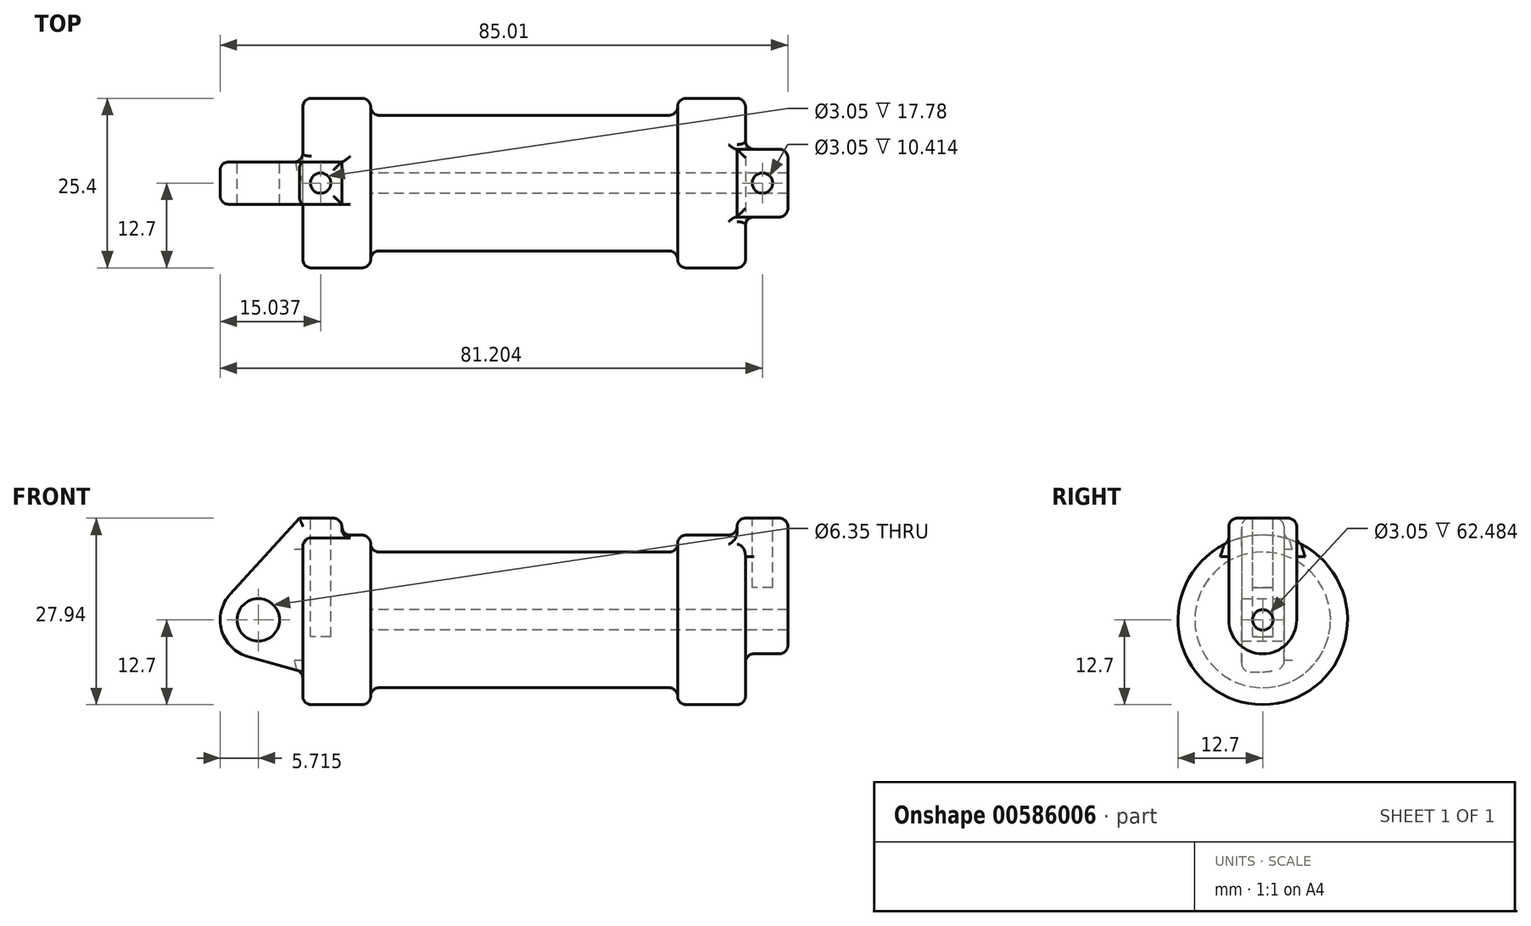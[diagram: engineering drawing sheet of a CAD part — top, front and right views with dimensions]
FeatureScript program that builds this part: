
annotation { "Feature Type Name" : "Feature", "Feature Type Description" : "" }
export const myFeature = defineFeature(function(context is Context, id is Id, definition is map)
    precondition{}
    {
        {
            var Q0;
            Q0=qCreatedBy(makeId("Front.planeOp"),FACE);
            var sketch = newSketch(context, id + "F0", { "sketchPlane" : qUnion([Q0])});
            skLineSegment(sketch, "E0", {"start": v(0, 0) * mm, "end": v(0, 12.7) * mm});
            skLineSegment(sketch, "E1", {"start": v(0, 12.7) * mm, "end": v(10.16, 12.7) * mm});
            skLineSegment(sketch, "E2", {"start": v(10.16, 12.7) * mm, "end": v(10.16, 10.16) * mm});
            skLineSegment(sketch, "E3", {"start": v(10.16, 10.16) * mm, "end": v(56.13, 10.16) * mm});
            skLineSegment(sketch, "E4", {"start": v(56.13, 10.16) * mm, "end": v(56.13, 12.7) * mm});
            skLineSegment(sketch, "E5", {"start": v(56.13, 12.7) * mm, "end": v(66.3, 12.7) * mm});
            skLineSegment(sketch, "E6", {"start": v(66.3, 12.7) * mm, "end": v(66.3, 0) * mm});
            skLineSegment(sketch, "E7", {"start": v(66.3, 0) * mm, "end": v(0, 0) * mm});
            skLineSegment(sketch, "E8", {"start": v(5.84, 15.24) * mm, "end": v(-0.5, 15.24) * mm});
            skLineSegment(sketch, "E9", {"start": v(-0.5, 15.24) * mm, "end": v(-10.88, 3.85) * mm});
            skLineSegment(sketch, "E10", {"start": v(0, 0) * mm, "end": v(-6.65, 0) * mm});
            skCircle(sketch, "E11", {"center": v(-6.65, 0) * mm, "radius": 5.72 * mm});
            skCircle(sketch, "E12", {"center": v(-6.65, 0) * mm, "radius": 3.18 * mm});
            skLineSegment(sketch, "E13", {"start": v(5.84, 15.24) * mm, "end": v(5.84, -9.4) * mm});
            skLineSegment(sketch, "E14", {"start": v(5.84, -9.4) * mm, "end": v(-8.18, -5.5) * mm});
            skSolve(sketch);
        }
        {
            var Q0;
            {var subQ0=sQuery(id+"F0.wireOp",EDGE,"E2");Q0=makeQuery(id+"F0.imprint","IMPRINT",FACE,{"disambiguationData":[TD([[makeQuery(id+"F0.imprint","IMPRINT",EDGE,{"derivedFrom":subQ0}),-1.0]])]});}
            var Q1;
            {var subQ0=sQuery(id+"F0.wireOp",EDGE,"E0");Q1=makeQuery(id+"F0.imprint","IMPRINT",FACE,{"disambiguationData":[TD([[makeQuery(id+"F0.imprint","IMPRINT",EDGE,{"derivedFrom":subQ0}),-1.0]])]});}
            var Q2;
            Q2=sQuery(id+"F0.wireOp",EDGE,"E7");
            revolve(context, id + "F1", {"entities" : qUnion([Q0, Q1]), "axis" : qUnion([Q2]), "revolveType" : RevolveType.FULL});
        }
        {
            var Q0;
            {var subQ1=sQuery(id+"F0.wireOp",EDGE,"E0");Q0=makeQuery(id+"F0.imprint","IMPRINT",FACE,{"disambiguationData":[TD([[makeQuery(id+"F0.imprint","IMPRINT",EDGE,{"derivedFrom":subQ1}),1.0]])]});}
            var Q1;
            {var subQ5=sQuery(id+"F0.wireOp",EDGE,"E12");Q1=makeQuery(id+"F0.imprint","IMPRINT",FACE,{"disambiguationData":[TD([[makeQuery(id+"F0.imprint","IMPRINT",EDGE,{"derivedFrom":subQ5}),-1.0]])]});}
            var Q2;
            {var subQ0=sQuery(id+"F0.wireOp",EDGE,"E14");Q2=makeQuery(id+"F0.imprint","IMPRINT",FACE,{"disambiguationData":[TD([[makeQuery(id+"F0.imprint","IMPRINT",EDGE,{"derivedFrom":subQ0}),-1.0]])]});}
            var Q3;
            {var subQ0=sQuery(id+"F0.wireOp",EDGE,"E0");Q3=makeQuery(id+"F0.imprint","IMPRINT",FACE,{"disambiguationData":[TD([[makeQuery(id+"F0.imprint","IMPRINT",EDGE,{"derivedFrom":subQ0}),-1.0]])]});}
            extrude(context, id + "F2", {"entities" : qUnion([Q0, Q1, Q2, Q3]), "operationType" : NewBodyOperationType.ADD, "endBound" : BoundingType.SYMMETRIC, "depth" : 6.35 * mm, "offsetDistance" : 25.4 * mm});
        }
        {
            var Q0;
            Q0=makeQuery(id+"F1.opRevolve","SWEPT_FACE",FACE,{"disambiguationData":[OSD([sQuery(id+"F0.wireOp",EDGE,"E6")])]});
            var sketch = newSketch(context, id + "F3", { "sketchPlane" : qUnion([Q0])});
            skCircle(sketch, "E15", {"center": v(0, 0) * mm, "radius": 1.52 * mm});
            skCircle(sketch, "E16", {"center": v(0, 0) * mm, "radius": 5.08 * mm});
            skLineSegment(sketch, "E17", {"start": v(-5.08, 0) * mm, "end": v(-5.08, 15.24) * mm});
            skLineSegment(sketch, "E18", {"start": v(-5.08, 15.24) * mm, "end": v(5.08, 15.24) * mm});
            skLineSegment(sketch, "E19", {"start": v(5.08, 15.24) * mm, "end": v(5.08, 0) * mm});
            skSolve(sketch);
        }
        {
            var Q0;
            {var subQ0=sQuery(id+"F3.wireOp",EDGE,"E18");Q0=makeQuery(id+"F3.imprint","IMPRINT",FACE,{"disambiguationData":[TD([[makeQuery(id+"F3.imprint","IMPRINT",EDGE,{"derivedFrom":subQ0}),-1.0]])]});}
            var Q1;
            {var subQ0=sQuery(id+"F3.wireOp",EDGE,"E17");var subQ1=sQuery(id+"F3.wireOp",EDGE,"E16");var subQ2=makeQuery(id+"F3.imprint","INTERSECT",VERTEX,{"derivedFrom":[subQ1,subQ0]});Q1=makeQuery(id+"F3.imprint","IMPRINT",FACE,{"disambiguationData":[TD([[makeQuery(id+"F3.imprint","IMPRINT",EDGE,{"disambiguationData":[TD([[subQ2,1.0]])],"derivedFrom":subQ1}),-1.0]])]});}
            var Q2;
            Q2=makeQuery(id+"F3.imprint","IMPRINT",FACE,{"disambiguationData":[TD([[makeQuery(id+"F3.imprint","IMPRINT",EDGE,{"derivedFrom":sQuery(id+"F3.wireOp",EDGE,"E15")}),-1.0]])]});
            extrude(context, id + "F4", {"entities" : qUnion([Q0, Q1, Q2]), "operationType" : NewBodyOperationType.ADD, "depth" : 6.35 * mm, "offsetDistance" : 25.4 * mm});
        }
        {
            var Q0;
            Q0 = qSketchRegion(id + "F3", true);
            extrude(context, id + "F5", {"entities" : qUnion([Q0]), "operationType" : NewBodyOperationType.ADD, "oppositeDirection" : true, "depth" : 1.27 * mm, "offsetDistance" : 25.4 * mm});
        }
        {
            var Q0;
            Q0=makeQuery(id+"F4.boolean.opBoolean","SPLIT",FACE,{"disambiguationData":[TD([makeQuery(id+"F4.opExtrude","SWEPT_FACE",FACE,{"disambiguationData":[OSD([sQuery(id+"F3.wireOp",EDGE,"E15")])]})])],"derivedFrom":makeQuery(id+"F1.opRevolve","SWEPT_FACE",FACE,{"disambiguationData":[OSD([sQuery(id+"F0.wireOp",EDGE,"E6")])]})});
            var Q1;
            Q1=makeQuery(id+"F1.opRevolve","SWEPT_FACE",FACE,{"disambiguationData":[OSD([sQuery(id+"F0.wireOp",EDGE,"E2")])]});
            extrude(context, id + "F6", {"entities" : qUnion([Q0]), "operationType" : NewBodyOperationType.REMOVE, "endBound" : BoundingType.UP_TO_SURFACE, "oppositeDirection" : true, "depth" : 25.4 * mm, "endBoundEntityFace" : qUnion([Q1]), "offsetDistance" : 25.4 * mm});
        }
        {
            var Q0;
            Q0=makeQuery(id+"F2.opExtrude","SWEPT_FACE",FACE,{"disambiguationData":[OSD([sQuery(id+"F0.wireOp",EDGE,"E8")])]});
            var sketch = newSketch(context, id + "F7", { "sketchPlane" : qUnion([Q0])});
            skCircle(sketch, "E20", {"center": v(2.67, 0) * mm, "radius": 1.52 * mm});
            skPoint(sketch, "E20.centerSnap0", {"position": v(2.67, 3.18) * mm});
            skPoint(sketch, "E20.centerSnap1", {"position": v(5.84, 0) * mm});
            skSolve(sketch);
        }
        {
            var Q0;
            Q0=makeQuery(id+"F7.imprint","IMPRINT",FACE,{"disambiguationData":[TD([[makeQuery(id+"F7.imprint","IMPRINT",EDGE,{"derivedFrom":sQuery(id+"F7.wireOp",EDGE,"E20")}),1.0]])]});
            extrude(context, id + "F8", {"entities" : qUnion([Q0]), "operationType" : NewBodyOperationType.REMOVE, "oppositeDirection" : true, "depth" : 17.78 * mm, "offsetDistance" : 25.4 * mm});
        }
        {
            var Q0;
            {var subQ0=sQuery(id+"F3.wireOp",EDGE,"E18");Q0=makeQuery(id+"F5.boolean.opBoolean","MERGE",FACE,{"derivedFrom":[makeQuery(id+"F4.opExtrude","SWEPT_FACE",FACE,{"disambiguationData":[OSD([subQ0])]}),makeQuery(id+"F5.opExtrude","SWEPT_FACE",FACE,{"disambiguationData":[OSD([subQ0])]})]});}
            var sketch = newSketch(context, id + "F9", { "sketchPlane" : qUnion([Q0])});
            skCircle(sketch, "E21", {"center": v(68.83, 0) * mm, "radius": 1.52 * mm});
            skPoint(sketch, "E21.centerSnap0", {"position": v(72.64, 0) * mm});
            skPoint(sketch, "E21.centerSnap1", {"position": v(68.83, 5.08) * mm});
            skSolve(sketch);
        }
        {
            var Q0;
            Q0=makeQuery(id+"F9.imprint","IMPRINT",FACE,{"disambiguationData":[TD([[makeQuery(id+"F9.imprint","IMPRINT",EDGE,{"derivedFrom":sQuery(id+"F9.wireOp",EDGE,"E21")}),1.0]])]});
            extrude(context, id + "F10", {"entities" : qUnion([Q0]), "operationType" : NewBodyOperationType.REMOVE, "oppositeDirection" : true, "depth" : 10.4 * mm, "offsetDistance" : 25.4 * mm});
        }
        {
            var Q0;
            {var subQ0=sQuery(id+"F0.wireOp",EDGE,"E5");var subQ1=sQuery(id+"F0.wireOp",EDGE,"E6");Q0=makeQuery(id+"F4.boolean.opBoolean","SPLIT",EDGE,{"disambiguationData":[topologyDisambiguationEdgeConnected([makeQuery(id+"F1.opRevolve","SWEPT_FACE",FACE,{"disambiguationData":[OSD([subQ1])]})])],"derivedFrom":makeQuery(id+"F1.opRevolve","SWEPT_EDGE",EDGE,{"disambiguationData":[OSD([subQ0,subQ1])]})});}
            var Q1;
            Q1=makeQuery(id+"F1.opRevolve","SWEPT_EDGE",EDGE,{"disambiguationData":[OSD([sQuery(id+"F0.wireOp",EDGE,"E4"),sQuery(id+"F0.wireOp",EDGE,"E5")])]});
            var Q2;
            Q2=makeQuery(id+"F1.opRevolve","SWEPT_EDGE",EDGE,{"disambiguationData":[OSD([sQuery(id+"F0.wireOp",EDGE,"E1"),sQuery(id+"F0.wireOp",EDGE,"E2")])]});
            var Q3;
            Q3=makeQuery(id+"F1.opRevolve","SWEPT_EDGE",EDGE,{"disambiguationData":[OSD([sQuery(id+"F0.wireOp",EDGE,"E0"),sQuery(id+"F0.wireOp",EDGE,"E1")])]});
            var Q4;
            Q4=makeQuery(id+"F1.opRevolve","SWEPT_EDGE",EDGE,{"disambiguationData":[OSD([sQuery(id+"F0.wireOp",EDGE,"E2"),sQuery(id+"F0.wireOp",EDGE,"E3")])]});
            var Q5;
            Q5=makeQuery(id+"F1.opRevolve","SWEPT_EDGE",EDGE,{"disambiguationData":[OSD([sQuery(id+"F0.wireOp",EDGE,"E3"),sQuery(id+"F0.wireOp",EDGE,"E4")])]});
            fillet(context, id + "F11", {"entities" : qUnion([Q0, Q1, Q2, Q3, Q4, Q5]), "radius" : 1.27 * mm, "tangentPropagation" : true, "allowEdgeOverflow" : false});
        }
        {
            var Q0;
            Q0=makeQuery(id+"F4.opExtrude","CAP_EDGE",EDGE,{"disambiguationData":[OSD([sQuery(id+"F3.wireOp",EDGE,"E18")])],"isStart":false});
            var Q1;
            {var subQ0=sQuery(id+"F3.wireOp",EDGE,"E18");var subQ1=sQuery(id+"F3.wireOp",EDGE,"E17");Q1=makeQuery(id+"F5.boolean.opBoolean","MERGE",EDGE,{"derivedFrom":[makeQuery(id+"F4.opExtrude","SWEPT_EDGE",EDGE,{"disambiguationData":[OSD([subQ1,subQ0])]}),makeQuery(id+"F5.opExtrude","SWEPT_EDGE",EDGE,{"disambiguationData":[OSD([subQ1,subQ0])]})]});}
            var Q2;
            Q2=makeQuery(id+"F4.opExtrude","CAP_EDGE",EDGE,{"disambiguationData":[OSD([sQuery(id+"F3.wireOp",EDGE,"E17")])],"isStart":false});
            var Q3;
            Q3=makeQuery(id+"F4.opExtrude","CAP_EDGE",EDGE,{"disambiguationData":[OSD([sQuery(id+"F3.wireOp",EDGE,"E16")])],"isStart":false});
            var Q4;
            {var subQ0=sQuery(id+"F3.wireOp",EDGE,"E17");Q4=makeQuery(id+"F4.boolean.opBoolean","SPLIT",EDGE,{"disambiguationData":[topologyDisambiguationEdgeConnected([makeQuery(id+"F1.opRevolve","SWEPT_FACE",FACE,{"disambiguationData":[OSD([sQuery(id+"F0.wireOp",EDGE,"E6")])]})])],"derivedFrom":makeQuery(id+"F4.opExtrude","CAP_EDGE",EDGE,{"disambiguationData":[OSD([subQ0])],"isStart":true})});}
            var Q5;
            {var subQ0=sQuery(id+"F3.wireOp",EDGE,"E17");var subQ1=sQuery(id+"F0.wireOp",EDGE,"E5");var subQ2=sQuery(id+"F0.wireOp",EDGE,"E6");Q5=makeQuery(id+"F11.opFillet","BLEND_EDGE",EDGE,{"blendedFrom":[makeQuery(id+"F4.boolean.opBoolean","SPLIT",EDGE,{"disambiguationData":[topologyDisambiguationEdgeConnected([makeQuery(id+"F1.opRevolve","SWEPT_FACE",FACE,{"disambiguationData":[OSD([subQ2])]})])],"derivedFrom":makeQuery(id+"F1.opRevolve","SWEPT_EDGE",EDGE,{"disambiguationData":[OSD([subQ1,subQ2])]})}),makeQuery(id+"F5.boolean.opBoolean","MERGE",FACE,{"derivedFrom":[makeQuery(id+"F4.opExtrude","SWEPT_FACE",FACE,{"disambiguationData":[OSD([subQ0])]}),makeQuery(id+"F5.opExtrude","SWEPT_FACE",FACE,{"disambiguationData":[OSD([subQ0])]})]})],"blendedInto":[makeQuery(id+"F5.boolean.opBoolean","MERGE",FACE,{"derivedFrom":[makeQuery(id+"F4.opExtrude","SWEPT_FACE",FACE,{"disambiguationData":[OSD([subQ0])]}),makeQuery(id+"F5.opExtrude","SWEPT_FACE",FACE,{"disambiguationData":[OSD([subQ0])]})]})]});}
            var Q6;
            Q6=makeQuery(id+"F5.boolean.opBoolean","INTERSECT",EDGE,{"derivedFrom":[makeQuery(id+"F1.opRevolve","SWEPT_FACE",FACE,{"disambiguationData":[OSD([sQuery(id+"F0.wireOp",EDGE,"E5")])]}),makeQuery(id+"F5.opExtrude","CAP_FACE",FACE,{"disambiguationData":[OSD([sQuery(id+"F3.wireOp",EDGE,"E15"),sQuery(id+"F3.wireOp",EDGE,"E16"),sQuery(id+"F3.wireOp",EDGE,"E17"),sQuery(id+"F3.wireOp",EDGE,"E18"),sQuery(id+"F3.wireOp",EDGE,"E19")])],"isStart":false})]});
            var Q7;
            {var subQ0=sQuery(id+"F3.wireOp",EDGE,"E19");var subQ1=sQuery(id+"F3.wireOp",EDGE,"E18");Q7=makeQuery(id+"F5.boolean.opBoolean","MERGE",EDGE,{"derivedFrom":[makeQuery(id+"F4.opExtrude","SWEPT_EDGE",EDGE,{"disambiguationData":[OSD([subQ1,subQ0])]}),makeQuery(id+"F5.opExtrude","SWEPT_EDGE",EDGE,{"disambiguationData":[OSD([subQ1,subQ0])]})]});}
            var Q8;
            Q8=makeQuery(id+"F5.opExtrude","CAP_EDGE",EDGE,{"disambiguationData":[OSD([sQuery(id+"F3.wireOp",EDGE,"E18")])],"isStart":false});
            fillet(context, id + "F12", {"entities" : qUnion([Q0, Q1, Q2, Q3, Q4, Q5, Q6, Q7, Q8]), "radius" : 1.27 * mm, "tangentPropagation" : true, "allowEdgeOverflow" : false});
        }
        {
            var Q0;
            Q0=makeQuery(id+"F2.opExtrude","CAP_EDGE",EDGE,{"disambiguationData":[OSD([sQuery(id+"F0.wireOp",EDGE,"E9")])],"isStart":false});
            var Q1;
            Q1=makeQuery(id+"F2.opExtrude","CAP_EDGE",EDGE,{"disambiguationData":[OSD([sQuery(id+"F0.wireOp",EDGE,"E11")])],"isStart":false});
            var Q2;
            Q2=makeQuery(id+"F2.opExtrude","CAP_EDGE",EDGE,{"disambiguationData":[OSD([sQuery(id+"F0.wireOp",EDGE,"E8")])],"isStart":false});
            var Q3;
            Q3=makeQuery(id+"F2.opExtrude","SWEPT_EDGE",EDGE,{"disambiguationData":[OSD([sQuery(id+"F0.wireOp",EDGE,"E8"),sQuery(id+"F0.wireOp",EDGE,"E13")])]});
            var Q4;
            Q4=makeQuery(id+"F2.opExtrude","CAP_EDGE",EDGE,{"disambiguationData":[OSD([sQuery(id+"F0.wireOp",EDGE,"E8")])],"isStart":true});
            var Q5;
            Q5=makeQuery(id+"F2.opExtrude","CAP_EDGE",EDGE,{"disambiguationData":[OSD([sQuery(id+"F0.wireOp",EDGE,"E9")])],"isStart":true});
            var Q6;
            Q6=makeQuery(id+"F2.boolean.opBoolean","INTERSECT",EDGE,{"derivedFrom":[makeQuery(id+"F1.opRevolve","SWEPT_FACE",FACE,{"disambiguationData":[OSD([sQuery(id+"F0.wireOp",EDGE,"E0")])]}),makeQuery(id+"F2.opExtrude","CAP_FACE",FACE,{"disambiguationData":[OSD([sQuery(id+"F0.wireOp",EDGE,"E8"),sQuery(id+"F0.wireOp",EDGE,"E9"),sQuery(id+"F0.wireOp",EDGE,"E11"),sQuery(id+"F0.wireOp",EDGE,"E12"),sQuery(id+"F0.wireOp",EDGE,"E13"),sQuery(id+"F0.wireOp",EDGE,"E14")])],"isStart":true})]});
            var Q7;
            Q7=makeQuery(id+"F11.opFillet","BLEND_EDGE",EDGE,{"blendedFrom":[makeQuery(id+"F1.opRevolve","SWEPT_EDGE",EDGE,{"disambiguationData":[OSD([sQuery(id+"F0.wireOp",EDGE,"E0"),sQuery(id+"F0.wireOp",EDGE,"E1")])]}),makeQuery(id+"F2.opExtrude","CAP_FACE",FACE,{"disambiguationData":[OSD([sQuery(id+"F0.wireOp",EDGE,"E8"),sQuery(id+"F0.wireOp",EDGE,"E9"),sQuery(id+"F0.wireOp",EDGE,"E11"),sQuery(id+"F0.wireOp",EDGE,"E12"),sQuery(id+"F0.wireOp",EDGE,"E13"),sQuery(id+"F0.wireOp",EDGE,"E14")])],"isStart":true})],"blendedInto":[makeQuery(id+"F2.opExtrude","CAP_FACE",FACE,{"disambiguationData":[OSD([sQuery(id+"F0.wireOp",EDGE,"E8"),sQuery(id+"F0.wireOp",EDGE,"E9"),sQuery(id+"F0.wireOp",EDGE,"E11"),sQuery(id+"F0.wireOp",EDGE,"E12"),sQuery(id+"F0.wireOp",EDGE,"E13"),sQuery(id+"F0.wireOp",EDGE,"E14")])],"isStart":true})]});
            var Q8;
            Q8=makeQuery(id+"F2.boolean.opBoolean","INTERSECT",EDGE,{"derivedFrom":[makeQuery(id+"F1.opRevolve","SWEPT_FACE",FACE,{"disambiguationData":[OSD([sQuery(id+"F0.wireOp",EDGE,"E1")])]}),makeQuery(id+"F2.opExtrude","SWEPT_FACE",FACE,{"disambiguationData":[OSD([sQuery(id+"F0.wireOp",EDGE,"E13")])]})]});
            fillet(context, id + "F13", {"entities" : qUnion([Q0, Q1, Q2, Q3, Q4, Q5, Q6, Q7, Q8]), "radius" : 1.27 * mm, "tangentPropagation" : true, "allowEdgeOverflow" : false});
        }
    });
